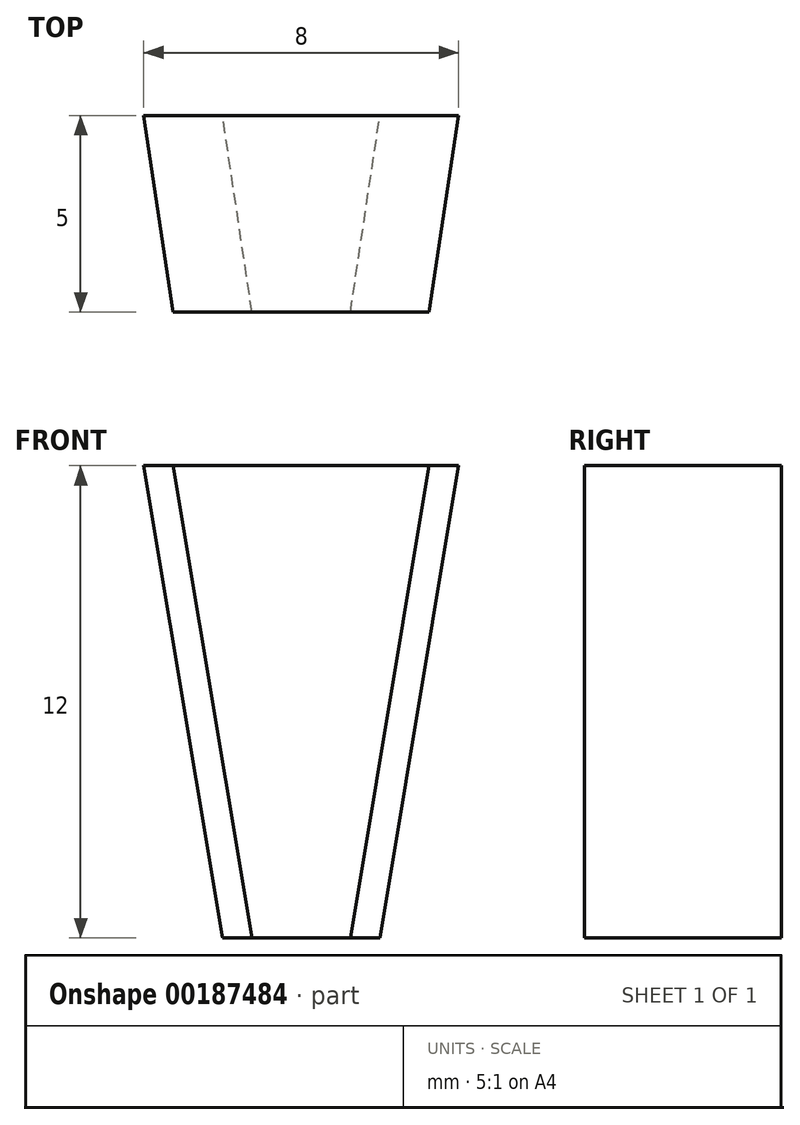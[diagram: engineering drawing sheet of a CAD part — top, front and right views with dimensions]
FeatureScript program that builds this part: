
annotation { "Feature Type Name" : "Feature", "Feature Type Description" : "" }
export const myFeature = defineFeature(function(context is Context, id is Id, definition is map)
    precondition{}
    {
        {
            var Q0;
            Q0=qCreatedBy(makeId("Front.planeOp"),FACE);
            cPlane(context, id + "F0", {"entities" : qUnion([Q0]), "cplaneType" : CPlaneType.OFFSET, "offset" : 5 * mm, "width" : 150 * mm, "height" : 150 * mm});
        }
        {
            var Q0;
            Q0=qCreatedBy(makeId("Front.planeOp"),FACE);
            var sketch = newSketch(context, id + "F1", { "sketchPlane" : qUnion([Q0])});
            skLineSegment(sketch, "E0", {"start": v(0, 12) * mm, "end": v(-4, 12) * mm});
            skLineSegment(sketch, "E1", {"start": v(-4, 12) * mm, "end": v(-2, 0) * mm});
            skLineSegment(sketch, "E2", {"start": v(-2, 0) * mm, "end": v(0, 0) * mm});
            skLineSegment(sketch, "E3.MirrorCS", {"start": v(0, 12) * mm, "end": v(4, 12) * mm});
            skLineSegment(sketch, "E4.MirrorCS", {"start": v(4, 12) * mm, "end": v(2, 0) * mm});
            skLineSegment(sketch, "E5.MirrorCS", {"start": v(2, 0) * mm, "end": v(0, 0) * mm});
            skSolve(sketch);
        }
        {
            var Q0;
            Q0=qCreatedBy(id+"F0.planeOp",FACE);
            var sketch = newSketch(context, id + "F2", { "sketchPlane" : qUnion([Q0])});
            skLineSegment(sketch, "E6", {"start": v(0, 0) * mm, "end": v(-1.25, 0) * mm});
            skLineSegment(sketch, "E7", {"start": v(-1.25, 0) * mm, "end": v(-3.25, 12) * mm});
            skLineSegment(sketch, "E8", {"start": v(-3.25, 12) * mm, "end": v(0, 12) * mm});
            skLineSegment(sketch, "E9.MirrorCS", {"start": v(3.25, 12) * mm, "end": v(0, 12) * mm});
            skLineSegment(sketch, "E10.MirrorCS", {"start": v(1.25, 0) * mm, "end": v(3.25, 12) * mm});
            skLineSegment(sketch, "E11.MirrorCS", {"start": v(0, 0) * mm, "end": v(1.25, 0) * mm});
            skSolve(sketch);
        }
        {
            var Q0;
            Q0=makeQuery(id+"F2.imprint","IMPRINT",FACE,{"disambiguationData":[TD([[makeQuery(id+"F2.imprint","IMPRINT",EDGE,{"derivedFrom":sQuery(id+"F2.wireOp",EDGE,"E6")}),-1.0]])]});
            var Q1;
            Q1=makeQuery(id+"F1.imprint","IMPRINT",FACE,{"disambiguationData":[TD([[makeQuery(id+"F1.imprint","IMPRINT",EDGE,{"derivedFrom":sQuery(id+"F1.wireOp",EDGE,"E0")}),1.0]])]});
            loft(context, id + "F3", {"sheetProfilesArray" : [{ "sheetProfileEntities" : qUnion([Q0]) }, { "sheetProfileEntities" : qUnion([Q1]) }]});
        }
    });
